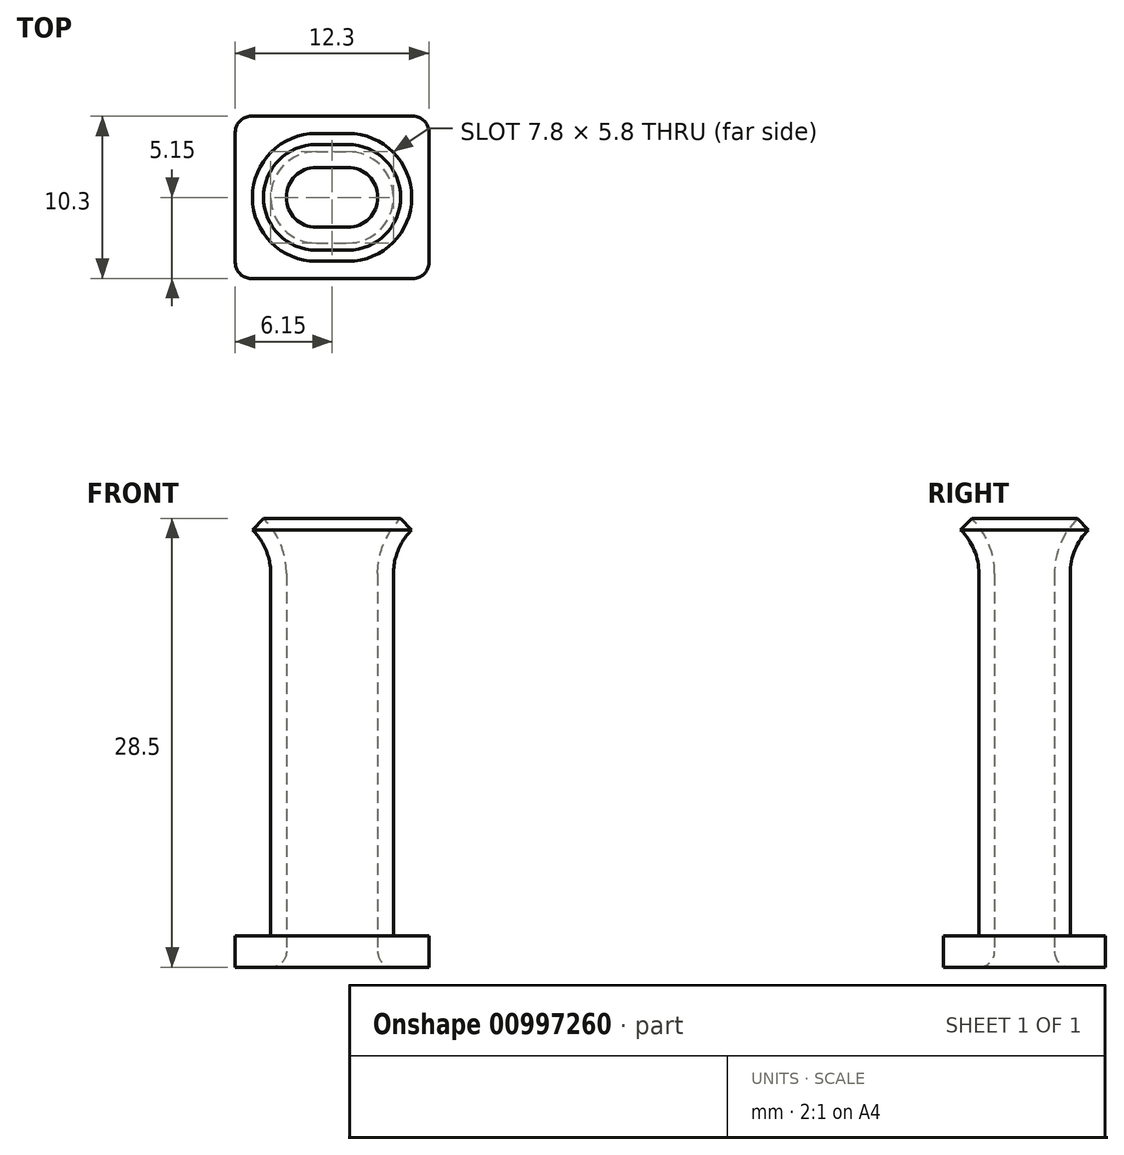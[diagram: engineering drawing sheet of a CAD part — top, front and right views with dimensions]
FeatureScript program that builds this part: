
annotation { "Feature Type Name" : "Feature", "Feature Type Description" : "" }
export const myFeature = defineFeature(function(context is Context, id is Id, definition is map)
    precondition{}
    {
        {
            var Q0;
            Q0=qCreatedBy(makeId("Top.planeOp"),FACE);
            var sketch = newSketch(context, id + "F0", { "sketchPlane" : qUnion([Q0])});
            skLineSegment(sketch, "E0.bottom", {"start": v(6.15, -5.15) * mm, "end": v(-6.15, -5.15) * mm});
            skLineSegment(sketch, "E0.top", {"start": v(6.15, 5.15) * mm, "end": v(-6.15, 5.15) * mm});
            skLineSegment(sketch, "E0.left", {"start": v(6.15, -5.15) * mm, "end": v(6.15, 5.15) * mm});
            skLineSegment(sketch, "E0.right", {"start": v(-6.15, -5.15) * mm, "end": v(-6.15, 5.15) * mm});
            skPoint(sketch, "E0.middle", {"position": v(0, 0) * mm});
            skLineSegment(sketch, "E1.bottom", {"start": v(2.9, -1.9) * mm, "end": v(-2.9, -1.9) * mm, "construction": true});
            skLineSegment(sketch, "E1.top", {"start": v(2.9, 1.9) * mm, "end": v(-2.9, 1.9) * mm, "construction": true});
            skLineSegment(sketch, "E1.left", {"start": v(2.9, -1.9) * mm, "end": v(2.9, 1.9) * mm, "construction": true});
            skLineSegment(sketch, "E1.right", {"start": v(-2.9, -1.9) * mm, "end": v(-2.9, 1.9) * mm, "construction": true});
            skArc(sketch, "E2", {"start": v(-1, 1.9) * mm, "mid": v(-2.9, 0) * mm, "end": v(-1, -1.9) * mm});
            skArc(sketch, "E3", {"start": v(1, -1.9) * mm, "mid": v(2.9, 0) * mm, "end": v(1, 1.9) * mm});
            skLineSegment(sketch, "E4", {"start": v(-1, 1.9) * mm, "end": v(1, 1.9) * mm});
            skLineSegment(sketch, "E5", {"start": v(-1, -1.9) * mm, "end": v(1, -1.9) * mm});
            skArc(sketch, "E6.0", {"start": v(1, -2.9) * mm, "mid": v(3.9, 0) * mm, "end": v(1, 2.9) * mm});
            skLineSegment(sketch, "E6.1", {"start": v(-1, -2.9) * mm, "end": v(1, -2.9) * mm});
            skArc(sketch, "E6.2", {"start": v(-1, 2.9) * mm, "mid": v(-3.9, 0) * mm, "end": v(-1, -2.9) * mm});
            skLineSegment(sketch, "E6.3", {"start": v(-1, 2.9) * mm, "end": v(1, 2.9) * mm});
            skSolve(sketch);
        }
        {
            var Q0;
            Q0=makeQuery(id+"F0.imprint","IMPRINT",FACE,{"disambiguationData":[TD([[makeQuery(id+"F0.imprint","IMPRINT",EDGE,{"derivedFrom":sQuery(id+"F0.wireOp",EDGE,"E0.bottom")}),-1.0]])]});
            extrude(context, id + "F1", {"entities" : qUnion([Q0]), "depth" : 2 * mm, "offsetDistance" : 25 * mm});
        }
        {
            var Q0;
            Q0=makeQuery(id+"F0.imprint","IMPRINT",FACE,{"disambiguationData":[TD([[makeQuery(id+"F0.imprint","IMPRINT",EDGE,{"derivedFrom":sQuery(id+"F0.wireOp",EDGE,"E2")}),-1.0]])]});
            extrude(context, id + "F2", {"entities" : qUnion([Q0]), "operationType" : NewBodyOperationType.ADD, "depth" : 25 * mm, "offsetDistance" : 25 * mm});
        }
        {
            var Q0;
            Q0=makeQuery(id+"F1.opExtrude","CAP_EDGE",EDGE,{"disambiguationData":[OSD([sQuery(id+"F0.wireOp",EDGE,"E6.2")])],"isStart":false});
            var Q1;
            Q1=makeQuery(id+"F1.opExtrude","SWEPT_EDGE",EDGE,{"disambiguationData":[OSD([sQuery(id+"F0.wireOp",EDGE,"E0.top"),sQuery(id+"F0.wireOp",EDGE,"E0.right")])]});
            var Q2;
            Q2=makeQuery(id+"F1.opExtrude","SWEPT_EDGE",EDGE,{"disambiguationData":[OSD([sQuery(id+"F0.wireOp",EDGE,"E0.top"),sQuery(id+"F0.wireOp",EDGE,"E0.left")])]});
            var Q3;
            Q3=makeQuery(id+"F1.opExtrude","SWEPT_EDGE",EDGE,{"disambiguationData":[OSD([sQuery(id+"F0.wireOp",EDGE,"E0.bottom"),sQuery(id+"F0.wireOp",EDGE,"E0.left")])]});
            var Q4;
            Q4=makeQuery(id+"F1.opExtrude","SWEPT_EDGE",EDGE,{"disambiguationData":[OSD([sQuery(id+"F0.wireOp",EDGE,"E0.bottom"),sQuery(id+"F0.wireOp",EDGE,"E0.right")])]});
            var Q5;
            Q5=makeQuery(id+"F2.opExtrude","CAP_EDGE",EDGE,{"disambiguationData":[OSD([sQuery(id+"F0.wireOp",EDGE,"E3")])],"isStart":true});
            fillet(context, id + "F3", {"entities" : qUnion([Q0, Q1, Q2, Q3, Q4, Q5]), "radius" : 1 * mm, "tangentPropagation" : true, "allowEdgeOverflow" : false});
        }
        {
            var Q0;
            Q0=qCreatedBy(makeId("Front.planeOp"),FACE);
            var sketch = newSketch(context, id + "F4", { "sketchPlane" : qUnion([Q0])});
            skPoint(sketch, "E7.0", {"position": v(2.9, 25) * mm});
            skPoint(sketch, "E8.0", {"position": v(3.9, 25) * mm});
            skLineSegment(sketch, "E9", {"start": v(2.9, 25) * mm, "end": v(3.9, 25) * mm});
            skLineSegment(sketch, "E10", {"start": v(3.9, 25) * mm, "end": v(3.9, 3) * mm});
            skArc(sketch, "E11", {"start": v(3.9, 25) * mm, "mid": v(4.2, 26.5) * mm, "end": v(5.06, 27.79) * mm});
            skArc(sketch, "E12.0", {"start": v(2.9, 25) * mm, "mid": v(3.28, 26.9) * mm, "end": v(4.36, 28.5) * mm});
            skLineSegment(sketch, "E13", {"start": v(4.36, 28.5) * mm, "end": v(5.06, 27.79) * mm});
            skSolve(sketch);
        }
        {
            var Q0;
            Q0=makeQuery(id+"F4.imprint","IMPRINT",FACE,{"disambiguationData":[TD([[makeQuery(id+"F4.imprint","IMPRINT",EDGE,{"derivedFrom":sQuery(id+"F4.wireOp",EDGE,"E9")}),1.0]])]});
            var Q1;
            Q1=makeQuery(id+"F2.opExtrude","CAP_EDGE",EDGE,{"disambiguationData":[OSD([sQuery(id+"F0.wireOp",EDGE,"E4")])],"isStart":false});
            var Q2;
            Q2=makeQuery(id+"F2.opExtrude","CAP_EDGE",EDGE,{"disambiguationData":[OSD([sQuery(id+"F0.wireOp",EDGE,"E2")])],"isStart":false});
            var Q3;
            Q3=makeQuery(id+"F2.opExtrude","CAP_EDGE",EDGE,{"disambiguationData":[OSD([sQuery(id+"F0.wireOp",EDGE,"E5")])],"isStart":false});
            var Q4;
            Q4=makeQuery(id+"F2.opExtrude","CAP_EDGE",EDGE,{"disambiguationData":[OSD([sQuery(id+"F0.wireOp",EDGE,"E3")])],"isStart":false});
            sweep(context, id + "F5", {"operationType" : NewBodyOperationType.ADD, "profiles" : qUnion([Q0]), "path" : qUnion([Q1, Q2, Q3, Q4])});
        }
    });
